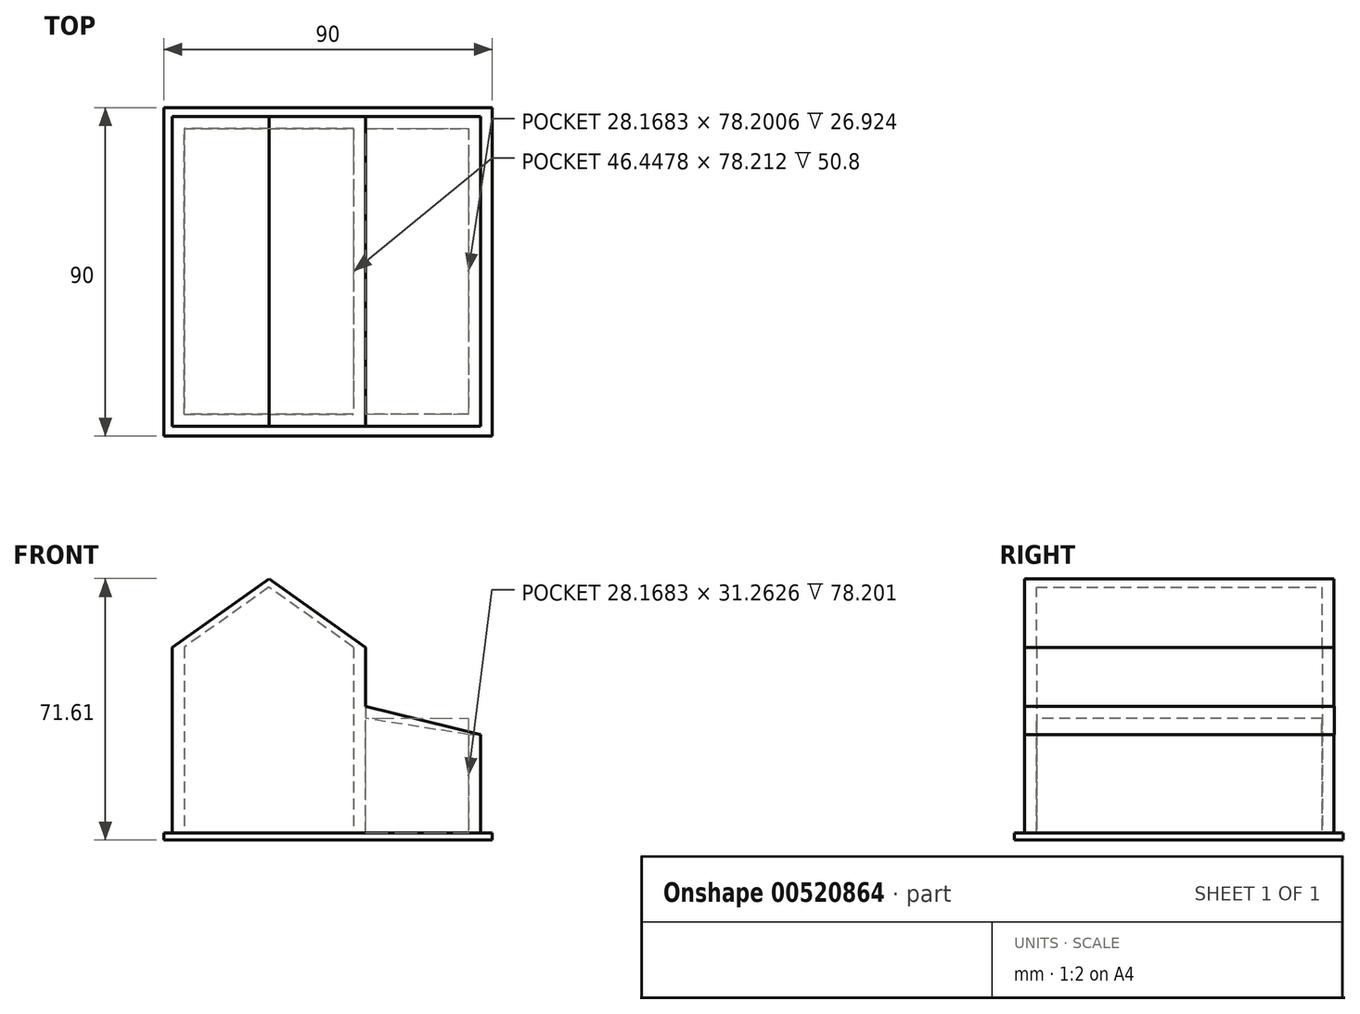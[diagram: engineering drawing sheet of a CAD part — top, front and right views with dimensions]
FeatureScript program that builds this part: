
annotation { "Feature Type Name" : "Feature", "Feature Type Description" : "" }
export const myFeature = defineFeature(function(context is Context, id is Id, definition is map)
    precondition{}
    {
        {
            var Q0;
            Q0=qCreatedBy(makeId("Top.planeOp"),FACE);
            var sketch = newSketch(context, id + "F0", { "sketchPlane" : qUnion([Q0])});
            skLineSegment(sketch, "E0.bottom", {"start": v(-45, 45) * mm, "end": v(45, 45) * mm});
            skLineSegment(sketch, "E0.top", {"start": v(-45, -45) * mm, "end": v(45, -45) * mm});
            skLineSegment(sketch, "E0.left", {"start": v(-45, 45) * mm, "end": v(-45, -45) * mm});
            skLineSegment(sketch, "E0.right", {"start": v(45, 45) * mm, "end": v(45, -45) * mm});
            skPoint(sketch, "E0.middle", {"position": v(0, 0) * mm});
            skSolve(sketch);
        }
        {
            var Q0;
            Q0 = qSketchRegion(id + "F0", true);
            extrude(context, id + "F1", {"entities" : qUnion([Q0]), "depth" : 2 * mm, "offsetDistance" : 25.4 * mm});
        }
        {
            var Q0;
            Q0=makeQuery(id+"F1.opExtrude","CAP_FACE",FACE,{"disambiguationData":[OSD([sQuery(id+"F0.wireOp",EDGE,"E0.bottom"),sQuery(id+"F0.wireOp",EDGE,"E0.top"),sQuery(id+"F0.wireOp",EDGE,"E0.left"),sQuery(id+"F0.wireOp",EDGE,"E0.right")])],"isStart":false});
            var sketch = newSketch(context, id + "F2", { "sketchPlane" : qUnion([Q0])});
            skLineSegment(sketch, "E1.bottom", {"start": v(-42.7, 42.55) * mm, "end": v(-39.4, 42.55) * mm});
            skLineSegment(sketch, "E1.top", {"start": v(-42.7, -42.25) * mm, "end": v(-39.4, -42.25) * mm});
            skLineSegment(sketch, "E1.left", {"start": v(-42.7, 42.55) * mm, "end": v(-42.7, -42.25) * mm});
            skLineSegment(sketch, "E1.right", {"start": v(-39.4, 42.55) * mm, "end": v(-39.4, -42.25) * mm});
            skSolve(sketch);
        }
        {
            var Q0;
            Q0 = qSketchRegion(id + "F2", true);
            extrude(context, id + "F3", {"entities" : qUnion([Q0]), "operationType" : NewBodyOperationType.ADD, "depth" : 50.8 * mm, "offsetDistance" : 25.4 * mm});
        }
        {
            var Q0;
            Q0=makeQuery(id+"F1.opExtrude","CAP_FACE",FACE,{"disambiguationData":[OSD([sQuery(id+"F0.wireOp",EDGE,"E0.bottom"),sQuery(id+"F0.wireOp",EDGE,"E0.top"),sQuery(id+"F0.wireOp",EDGE,"E0.left"),sQuery(id+"F0.wireOp",EDGE,"E0.right")])],"isStart":false});
            var sketch = newSketch(context, id + "F4", { "sketchPlane" : qUnion([Q0])});
            skLineSegment(sketch, "E2.bottom", {"start": v(-39.4, 42.55) * mm, "end": v(10.34, 42.55) * mm});
            skLineSegment(sketch, "E2.top", {"start": v(-39.4, 39.26) * mm, "end": v(10.34, 39.26) * mm});
            skLineSegment(sketch, "E2.left", {"start": v(-39.4, 42.55) * mm, "end": v(-39.4, 39.26) * mm});
            skLineSegment(sketch, "E2.right", {"start": v(10.34, 42.55) * mm, "end": v(10.34, 39.26) * mm});
            skSolve(sketch);
        }
        {
            var Q0;
            Q0 = qSketchRegion(id + "F4", true);
            extrude(context, id + "F5", {"entities" : qUnion([Q0]), "operationType" : NewBodyOperationType.ADD, "depth" : 50.8 * mm, "offsetDistance" : 25.4 * mm});
        }
        {
            var Q0;
            Q0=makeQuery(id+"F1.opExtrude","CAP_FACE",FACE,{"disambiguationData":[OSD([sQuery(id+"F0.wireOp",EDGE,"E0.bottom"),sQuery(id+"F0.wireOp",EDGE,"E0.top"),sQuery(id+"F0.wireOp",EDGE,"E0.left"),sQuery(id+"F0.wireOp",EDGE,"E0.right")])],"isStart":false});
            var sketch = newSketch(context, id + "F6", { "sketchPlane" : qUnion([Q0])});
            skLineSegment(sketch, "E3.bottom", {"start": v(-39.4, -42.25) * mm, "end": v(10.34, -42.25) * mm});
            skLineSegment(sketch, "E3.top", {"start": v(-39.4, -38.96) * mm, "end": v(10.34, -38.96) * mm});
            skLineSegment(sketch, "E3.left", {"start": v(-39.4, -42.25) * mm, "end": v(-39.4, -38.96) * mm});
            skLineSegment(sketch, "E3.right", {"start": v(10.34, -42.25) * mm, "end": v(10.34, -38.96) * mm});
            skSolve(sketch);
        }
        {
            var Q0;
            Q0 = qSketchRegion(id + "F6", true);
            extrude(context, id + "F7", {"entities" : qUnion([Q0]), "operationType" : NewBodyOperationType.ADD, "depth" : 50.8 * mm, "offsetDistance" : 25.4 * mm});
        }
        {
            var Q0;
            Q0=makeQuery(id+"F1.opExtrude","CAP_FACE",FACE,{"disambiguationData":[OSD([sQuery(id+"F0.wireOp",EDGE,"E0.bottom"),sQuery(id+"F0.wireOp",EDGE,"E0.top"),sQuery(id+"F0.wireOp",EDGE,"E0.left"),sQuery(id+"F0.wireOp",EDGE,"E0.right")])],"isStart":false});
            var sketch = newSketch(context, id + "F8", { "sketchPlane" : qUnion([Q0])});
            skLineSegment(sketch, "E4.bottom", {"start": v(10.34, 39.26) * mm, "end": v(7.04, 39.26) * mm});
            skLineSegment(sketch, "E4.top", {"start": v(10.34, -38.96) * mm, "end": v(7.04, -38.96) * mm});
            skLineSegment(sketch, "E4.left", {"start": v(10.34, 39.26) * mm, "end": v(10.34, -38.96) * mm});
            skLineSegment(sketch, "E4.right", {"start": v(7.04, 39.26) * mm, "end": v(7.04, -38.96) * mm});
            skSolve(sketch);
        }
        {
            var Q0;
            Q0 = qSketchRegion(id + "F8", true);
            extrude(context, id + "F9", {"entities" : qUnion([Q0]), "operationType" : NewBodyOperationType.ADD, "depth" : 50.8 * mm, "offsetDistance" : 25.4 * mm});
        }
        {
            var Q0;
            Q0=makeQuery(id+"F7.boolean.opBoolean","MERGE",FACE,{"derivedFrom":[makeQuery(id+"F3.opExtrude","SWEPT_FACE",FACE,{"disambiguationData":[OSD([sQuery(id+"F2.wireOp",EDGE,"E1.top")])]}),makeQuery(id+"F7.opExtrude","SWEPT_FACE",FACE,{"disambiguationData":[OSD([sQuery(id+"F6.wireOp",EDGE,"E3.bottom")])]})]});
            var sketch = newSketch(context, id + "F10", { "sketchPlane" : qUnion([Q0])});
            skLineSegment(sketch, "E5", {"start": v(-42.7, 52.8) * mm, "end": v(10.34, 52.8) * mm});
            skLineSegment(sketch, "E6", {"start": v(10.34, 52.8) * mm, "end": v(-16.18, 71.6) * mm});
            skLineSegment(sketch, "E7", {"start": v(-16.18, 71.6) * mm, "end": v(-42.7, 52.8) * mm});
            skSolve(sketch);
        }
        {
            var Q0;
            Q0 = qSketchRegion(id + "F10", true);
            extrude(context, id + "F11", {"entities" : qUnion([Q0]), "operationType" : NewBodyOperationType.ADD, "oppositeDirection" : true, "depth" : 3.3 * mm, "offsetDistance" : 25.4 * mm});
        }
        {
            var Q0;
            Q0=makeQuery(id+"F5.boolean.opBoolean","MERGE",FACE,{"derivedFrom":[makeQuery(id+"F3.opExtrude","SWEPT_FACE",FACE,{"disambiguationData":[OSD([sQuery(id+"F2.wireOp",EDGE,"E1.bottom")])]}),makeQuery(id+"F5.opExtrude","SWEPT_FACE",FACE,{"disambiguationData":[OSD([sQuery(id+"F4.wireOp",EDGE,"E2.bottom")])]})]});
            var sketch = newSketch(context, id + "F12", { "sketchPlane" : qUnion([Q0])});
            skLineSegment(sketch, "E8", {"start": v(-10.34, 52.8) * mm, "end": v(16.18, 71.6) * mm});
            skLineSegment(sketch, "E9", {"start": v(16.18, 71.6) * mm, "end": v(42.7, 52.8) * mm});
            skLineSegment(sketch, "E10", {"start": v(42.7, 52.8) * mm, "end": v(-10.34, 52.8) * mm});
            skSolve(sketch);
        }
        {
            var Q0;
            Q0 = qSketchRegion(id + "F12", true);
            extrude(context, id + "F13", {"entities" : qUnion([Q0]), "operationType" : NewBodyOperationType.ADD, "oppositeDirection" : true, "depth" : 3.3 * mm, "offsetDistance" : 25.4 * mm});
        }
        {
            var Q0;
            Q0=makeQuery(id+"F13.opExtrude","CAP_FACE",FACE,{"disambiguationData":[OSD([sQuery(id+"F12.wireOp",EDGE,"E8"),sQuery(id+"F12.wireOp",EDGE,"E9"),sQuery(id+"F12.wireOp",EDGE,"E10")])],"isStart":false});
            var sketch = newSketch(context, id + "F14", { "sketchPlane" : qUnion([Q0])});
            skLineSegment(sketch, "E11", {"start": v(-39.4, 52.8) * mm, "end": v(-16.2, 69.26) * mm});
            skLineSegment(sketch, "E12", {"start": v(-16.2, 69.26) * mm, "end": v(7.04, 52.8) * mm});
            skLineSegment(sketch, "E13", {"start": v(7.04, 52.8) * mm, "end": v(10.34, 52.8) * mm});
            skLineSegment(sketch, "E14", {"start": v(10.34, 52.8) * mm, "end": v(-16.18, 71.6) * mm});
            skLineSegment(sketch, "E15", {"start": v(-16.18, 71.6) * mm, "end": v(-42.7, 52.8) * mm});
            skLineSegment(sketch, "E16", {"start": v(-42.7, 52.8) * mm, "end": v(-39.4, 52.8) * mm});
            skSolve(sketch);
        }
        {
            var Q0;
            Q0 = qSketchRegion(id + "F14", true);
            extrude(context, id + "F15", {"entities" : qUnion([Q0]), "operationType" : NewBodyOperationType.ADD, "depth" : 78.74 * mm, "offsetDistance" : 25.4 * mm});
        }
        {
            var Q0;
            {var subQ0=sQuery(id+"F0.wireOp",EDGE,"E0.left");var subQ1=sQuery(id+"F0.wireOp",EDGE,"E0.bottom");var subQ2=sQuery(id+"F0.wireOp",EDGE,"E0.right");var subQ3=sQuery(id+"F0.wireOp",EDGE,"E0.top");Q0=makeQuery(id+"F9.boolean.opBoolean","SPLIT",FACE,{"disambiguationData":[TD([makeQuery(id+"F1.opExtrude","SWEPT_FACE",FACE,{"disambiguationData":[OSD([subQ1])]})])],"derivedFrom":makeQuery(id+"F1.opExtrude","CAP_FACE",FACE,{"disambiguationData":[OSD([subQ1,subQ3,subQ0,subQ2])],"isStart":false})});}
            var sketch = newSketch(context, id + "F16", { "sketchPlane" : qUnion([Q0])});
            skLineSegment(sketch, "E17.bottom", {"start": v(41.8, 42.55) * mm, "end": v(38.5, 42.55) * mm});
            skLineSegment(sketch, "E17.top", {"start": v(41.8, -42.25) * mm, "end": v(38.5, -42.25) * mm});
            skLineSegment(sketch, "E17.left", {"start": v(41.8, 42.55) * mm, "end": v(41.8, -42.25) * mm});
            skLineSegment(sketch, "E17.right", {"start": v(38.5, 42.55) * mm, "end": v(38.5, -42.25) * mm});
            skSolve(sketch);
        }
        {
            var Q0;
            Q0 = qSketchRegion(id + "F16", true);
            extrude(context, id + "F17", {"entities" : qUnion([Q0]), "operationType" : NewBodyOperationType.ADD, "depth" : 26.92 * mm, "offsetDistance" : 25.4 * mm});
        }
        {
            var Q0;
            Q0=makeQuery(id+"F17.opExtrude","SWEPT_FACE",FACE,{"disambiguationData":[OSD([sQuery(id+"F16.wireOp",EDGE,"E17.top")])]});
            var sketch = newSketch(context, id + "F18", { "sketchPlane" : qUnion([Q0])});
            skLineSegment(sketch, "E18", {"start": v(38.5, 2) * mm, "end": v(10.34, 2) * mm});
            skLineSegment(sketch, "E19", {"start": v(10.34, 2) * mm, "end": v(10.34, 33.26) * mm});
            skLineSegment(sketch, "E20", {"start": v(10.34, 33.26) * mm, "end": v(38.5, 28.92) * mm});
            skLineSegment(sketch, "E21", {"start": v(38.5, 28.92) * mm, "end": v(38.5, 2) * mm});
            skSolve(sketch);
        }
        {
            var Q0;
            Q0 = qSketchRegion(id + "F18", true);
            extrude(context, id + "F19", {"entities" : qUnion([Q0]), "operationType" : NewBodyOperationType.ADD, "oppositeDirection" : true, "depth" : 3.3 * mm, "offsetDistance" : 25.4 * mm});
        }
        {
            var Q0;
            Q0=makeQuery(id+"F17.opExtrude","SWEPT_FACE",FACE,{"disambiguationData":[OSD([sQuery(id+"F16.wireOp",EDGE,"E17.bottom")])]});
            var sketch = newSketch(context, id + "F20", { "sketchPlane" : qUnion([Q0])});
            skLineSegment(sketch, "E22", {"start": v(-38.5, 28.92) * mm, "end": v(-10.34, 33.26) * mm});
            skLineSegment(sketch, "E23", {"start": v(-10.34, 33.26) * mm, "end": v(-10.34, 2) * mm});
            skLineSegment(sketch, "E24", {"start": v(-10.34, 2) * mm, "end": v(-38.5, 2) * mm});
            skLineSegment(sketch, "E25", {"start": v(-38.5, 2) * mm, "end": v(-38.5, 28.92) * mm});
            skSolve(sketch);
        }
        {
            var Q0;
            Q0 = qSketchRegion(id + "F20", true);
            extrude(context, id + "F21", {"entities" : qUnion([Q0]), "operationType" : NewBodyOperationType.ADD, "oppositeDirection" : true, "depth" : 3.3 * mm, "offsetDistance" : 25.4 * mm});
        }
        {
            var Q0;
            Q0=makeQuery(id+"F19.boolean.opBoolean","MERGE",FACE,{"derivedFrom":[makeQuery(id+"F11.boolean.opBoolean","MERGE",FACE,{"derivedFrom":[makeQuery(id+"F7.boolean.opBoolean","MERGE",FACE,{"derivedFrom":[makeQuery(id+"F3.opExtrude","SWEPT_FACE",FACE,{"disambiguationData":[OSD([sQuery(id+"F2.wireOp",EDGE,"E1.top")])]}),makeQuery(id+"F7.opExtrude","SWEPT_FACE",FACE,{"disambiguationData":[OSD([sQuery(id+"F6.wireOp",EDGE,"E3.bottom")])]})]}),makeQuery(id+"F11.opExtrude","CAP_FACE",FACE,{"disambiguationData":[OSD([sQuery(id+"F10.wireOp",EDGE,"E5"),sQuery(id+"F10.wireOp",EDGE,"E6"),sQuery(id+"F10.wireOp",EDGE,"E7")])],"isStart":true})]}),makeQuery(id+"F17.opExtrude","SWEPT_FACE",FACE,{"disambiguationData":[OSD([sQuery(id+"F16.wireOp",EDGE,"E17.top")])]}),makeQuery(id+"F19.opExtrude","CAP_FACE",FACE,{"disambiguationData":[OSD([sQuery(id+"F18.wireOp",EDGE,"E18"),sQuery(id+"F18.wireOp",EDGE,"E19"),sQuery(id+"F18.wireOp",EDGE,"E20"),sQuery(id+"F18.wireOp",EDGE,"E21")])],"isStart":true})]});
            var sketch = newSketch(context, id + "F22", { "sketchPlane" : qUnion([Q0])});
            skLineSegment(sketch, "E26", {"start": v(10.34, 33.26) * mm, "end": v(10.34, 36.56) * mm});
            skLineSegment(sketch, "E27", {"start": v(10.34, 36.56) * mm, "end": v(41.8, 28.92) * mm});
            skLineSegment(sketch, "E28", {"start": v(41.8, 28.92) * mm, "end": v(38.5, 28.92) * mm});
            skLineSegment(sketch, "E29", {"start": v(38.5, 28.92) * mm, "end": v(10.34, 33.26) * mm});
            skSolve(sketch);
        }
        {
            var Q0;
            Q0 = qSketchRegion(id + "F22", true);
            extrude(context, id + "F23", {"entities" : qUnion([Q0]), "operationType" : NewBodyOperationType.ADD, "oppositeDirection" : true, "depth" : 84.84 * mm, "offsetDistance" : 25.4 * mm});
        }
    });
